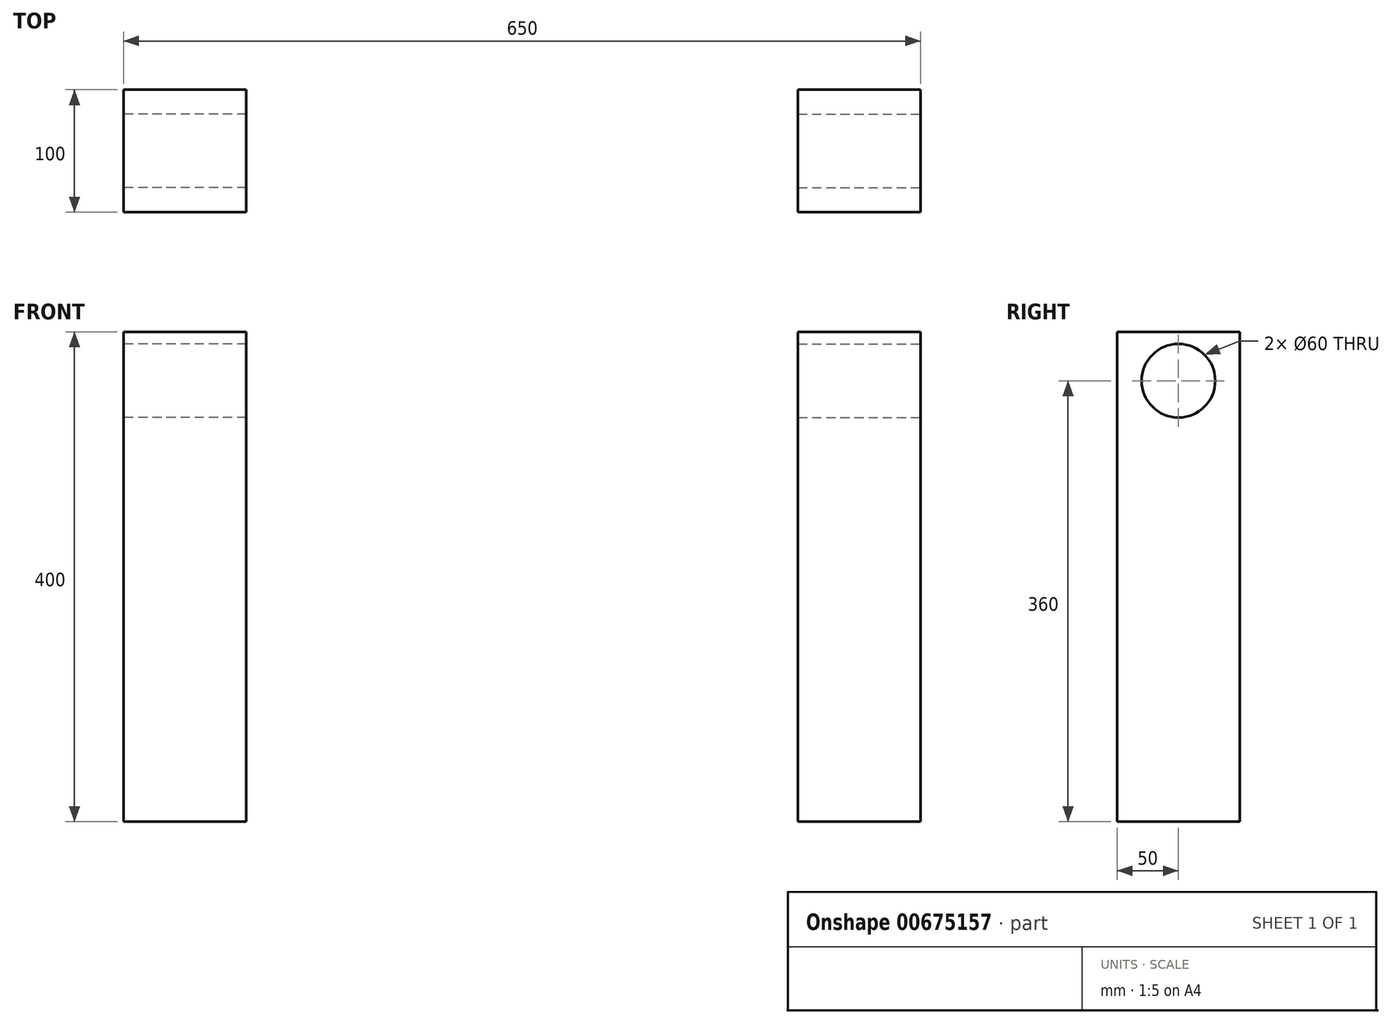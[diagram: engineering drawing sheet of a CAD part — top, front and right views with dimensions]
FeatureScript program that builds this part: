
annotation { "Feature Type Name" : "Feature", "Feature Type Description" : "" }
export const myFeature = defineFeature(function(context is Context, id is Id, definition is map)
    precondition{}
    {
        {
            var Q0;
            Q0=qCreatedBy(makeId("Top.planeOp"),FACE);
            var sketch = newSketch(context, id + "F0", { "sketchPlane" : qUnion([Q0])});
            skLineSegment(sketch, "E0.bottom", {"start": v(-325, 50) * mm, "end": v(-225, 50) * mm});
            skLineSegment(sketch, "E0.top", {"start": v(-325, -50) * mm, "end": v(-225, -50) * mm});
            skLineSegment(sketch, "E0.left", {"start": v(-325, 50) * mm, "end": v(-325, -50) * mm});
            skLineSegment(sketch, "E0.right", {"start": v(-225, 50) * mm, "end": v(-225, -50) * mm});
            skLineSegment(sketch, "E1.bottom", {"start": v(225, 50) * mm, "end": v(325, 50) * mm});
            skLineSegment(sketch, "E1.top", {"start": v(225, -50) * mm, "end": v(325, -50) * mm});
            skLineSegment(sketch, "E1.left", {"start": v(225, 50) * mm, "end": v(225, -50) * mm});
            skLineSegment(sketch, "E1.right", {"start": v(325, 50) * mm, "end": v(325, -50) * mm});
            skSolve(sketch);
        }
        {
            var Q0;
            Q0=makeQuery(id+"F0.imprint","IMPRINT",FACE,{"disambiguationData":[TD([[makeQuery(id+"F0.imprint","IMPRINT",EDGE,{"derivedFrom":sQuery(id+"F0.wireOp",EDGE,"E0.bottom")}),-1.0]])]});
            var Q1;
            Q1=makeQuery(id+"F0.imprint","IMPRINT",FACE,{"disambiguationData":[TD([[makeQuery(id+"F0.imprint","IMPRINT",EDGE,{"derivedFrom":sQuery(id+"F0.wireOp",EDGE,"E1.bottom")}),-1.0]])]});
            extrude(context, id + "F1", {"entities" : qUnion([Q0, Q1]), "depth" : 400 * mm, "offsetDistance" : 25 * mm});
        }
        {
            var Q0;
            Q0=makeQuery(id+"F1.opExtrude","SWEPT_FACE",FACE,{"disambiguationData":[OSD([sQuery(id+"F0.wireOp",EDGE,"E1.right")])]});
            var sketch = newSketch(context, id + "F2", { "sketchPlane" : qUnion([Q0])});
            skCircle(sketch, "E2", {"center": v(0, 360) * mm, "radius": 30 * mm});
            skSolve(sketch);
        }
        {
            var Q0;
            Q0=makeQuery(id+"F2.imprint","IMPRINT",FACE,{"disambiguationData":[TD([[makeQuery(id+"F2.imprint","IMPRINT",EDGE,{"derivedFrom":sQuery(id+"F2.wireOp",EDGE,"E2")}),1.0]])]});
            extrude(context, id + "F3", {"entities" : qUnion([Q0]), "operationType" : NewBodyOperationType.REMOVE, "oppositeDirection" : true, "depth" : 100 * mm, "offsetDistance" : 25 * mm});
        }
        {
            var Q0;
            Q0=makeQuery(id+"F1.opExtrude","SWEPT_FACE",FACE,{"disambiguationData":[OSD([sQuery(id+"F0.wireOp",EDGE,"E0.left")])]});
            var sketch = newSketch(context, id + "F4", { "sketchPlane" : qUnion([Q0])});
            skCircle(sketch, "E3", {"center": v(0, 360) * mm, "radius": 30 * mm});
            skSolve(sketch);
        }
        {
            var Q0;
            Q0=makeQuery(id+"F4.imprint","IMPRINT",FACE,{"disambiguationData":[TD([[makeQuery(id+"F4.imprint","IMPRINT",EDGE,{"derivedFrom":sQuery(id+"F4.wireOp",EDGE,"E3")}),1.0]])]});
            extrude(context, id + "F5", {"entities" : qUnion([Q0]), "operationType" : NewBodyOperationType.REMOVE, "oppositeDirection" : true, "depth" : 100 * mm, "offsetDistance" : 25 * mm});
        }
    });
